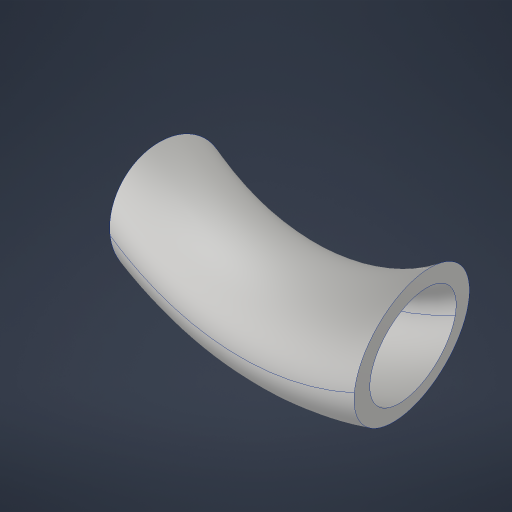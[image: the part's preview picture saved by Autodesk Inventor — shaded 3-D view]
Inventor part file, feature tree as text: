
AUTODESK INVENTOR PART (.ipt)
format: ipt  version: 2023.4 (Build 274418000, 418)  size: 299,520 bytes
history: native  units: in
note: dims shown in document units (in); Inventor stores cm internally (conversion verified against a paired STEP export)
features: sketch x5, projected_geometry x4, sweep x3, extrude x2
ambient origin geometry x8: Origin, YZ Plane, XZ Plane, XY Plane, X Axis, Y Axis, Z Axis, Center Point
bodies: Solid1 (feature_tree)
feature tree (14):
  extrude  "Extrusion1"  Depth=3.25in
  sketch  "Sketch2"  dims[d2=2.0in d3=0.0in d4=1.5in]
  sketch  "Sketch3"  dims[d5=3.75in d6=0.0in d7=0.0in]
  sweep  "Sweep1"
  sketch  "Sketch7"  dims[d20=0.25in d21=1.0in]
  sweep  "Sweep5"
  sweep  "Sweep6"
  extrude  "Extrusion3"  TaperAngle=0.0deg  [1 undecoded]
  sketch  "Sketch1"  dims[d0=4.0in d1=3.25in]
  sketch  "Sketch8"  dims[d22=1.0in d23=0.0in d24=0.0in d25=0.0in d26=0.0in d27=0.0in d28=0.0in]
  projected_geometry  "Project Cut Edges1"
  projected_geometry  "Project Cut Edges2"
  projected_geometry  "Project Cut Edges6"
  projected_geometry  "Project Cut Edges7"
note: 1 required parameter value undecoded (feature->parameter linkage not recoverable at this tier; creation-order binding heuristic only, values carry confidence <= 0.55)
